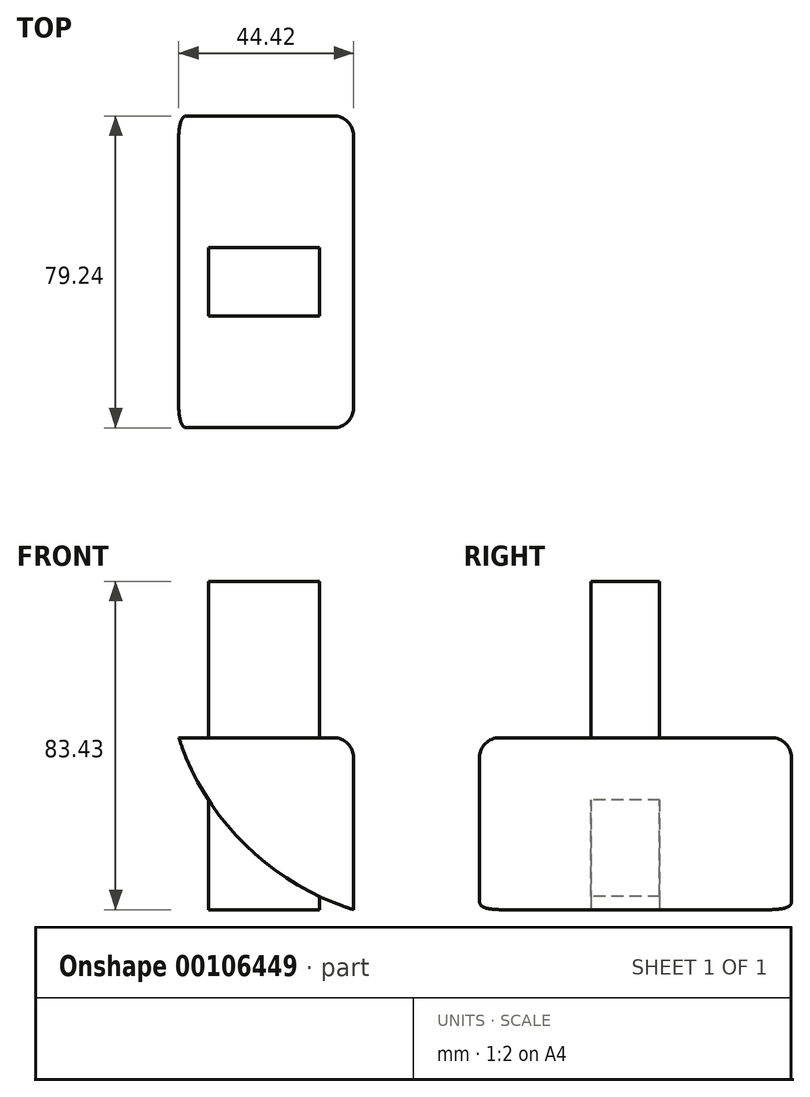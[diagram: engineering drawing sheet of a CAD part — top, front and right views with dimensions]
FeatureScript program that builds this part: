
annotation { "Feature Type Name" : "Feature", "Feature Type Description" : "" }
export const myFeature = defineFeature(function(context is Context, id is Id, definition is map)
    precondition{}
    {
        {
            var Q0;
            Q0=qCreatedBy(makeId("Front.planeOp"),FACE);
            var sketch = newSketch(context, id + "F0", { "sketchPlane" : qUnion([Q0])});
            skLineSegment(sketch, "E0.bottom", {"start": v(-21.73, 0) * mm, "end": v(26.08, 0) * mm});
            skLineSegment(sketch, "E0.top", {"start": v(-21.73, 43.68) * mm, "end": v(26.08, 43.68) * mm});
            skLineSegment(sketch, "E0.left", {"start": v(-21.73, 0) * mm, "end": v(-21.73, 43.68) * mm});
            skLineSegment(sketch, "E0.right", {"start": v(26.08, 0) * mm, "end": v(26.08, 43.68) * mm});
            skSolve(sketch);
        }
        {
            var Q0;
            Q0 = qSketchRegion(id + "F0", true);
            extrude(context, id + "F1", {"entities" : qUnion([Q0]), "depth" : 79.24 * mm});
        }
        {
            var Q0;
            Q0=makeQuery(id+"F1.opExtrude","SWEPT_EDGE",EDGE,{"disambiguationData":[OSD([sQuery(id+"F0.wireOp",EDGE,"E0.bottom"),sQuery(id+"F0.wireOp",EDGE,"E0.left")])]});
            fillet(context, id + "F2", {"entities" : qUnion([Q0]), "radius" : 67.93 * mm, "tangentPropagation" : true, "allowEdgeOverflow" : false});
        }
        {
            var Q0;
            Q0=makeQuery(id+"F1.opExtrude","SWEPT_EDGE",EDGE,{"disambiguationData":[OSD([sQuery(id+"F0.wireOp",EDGE,"E0.top"),sQuery(id+"F0.wireOp",EDGE,"E0.right")])]});
            var Q1;
            Q1=makeQuery(id+"F1.opExtrude","CAP_EDGE",EDGE,{"disambiguationData":[OSD([sQuery(id+"F0.wireOp",EDGE,"E0.top")])],"isStart":false});
            var Q2;
            Q2=makeQuery(id+"F1.opExtrude","CAP_EDGE",EDGE,{"disambiguationData":[OSD([sQuery(id+"F0.wireOp",EDGE,"E0.right")])],"isStart":false});
            var Q3;
            Q3=makeQuery(id+"F1.opExtrude","CAP_EDGE",EDGE,{"disambiguationData":[OSD([sQuery(id+"F0.wireOp",EDGE,"E0.right")])],"isStart":true});
            var Q4;
            Q4=makeQuery(id+"F1.opExtrude","CAP_EDGE",EDGE,{"disambiguationData":[OSD([sQuery(id+"F0.wireOp",EDGE,"E0.top")])],"isStart":true});
            fillet(context, id + "F3", {"entities" : qUnion([Q0, Q1, Q2, Q3, Q4]), "radius" : 5.08 * mm, "tangentPropagation" : true, "allowEdgeOverflow" : false});
        }
        {
            var Q0;
            Q0=qCreatedBy(makeId("Top.planeOp"),FACE);
            var sketch = newSketch(context, id + "F4", { "sketchPlane" : qUnion([Q0])});
            skLineSegment(sketch, "E1.bottom", {"start": v(-10.8, -33.5) * mm, "end": v(17.38, -33.5) * mm});
            skLineSegment(sketch, "E1.top", {"start": v(-10.8, -50.88) * mm, "end": v(17.38, -50.88) * mm});
            skLineSegment(sketch, "E1.left", {"start": v(-10.8, -33.5) * mm, "end": v(-10.8, -50.88) * mm});
            skLineSegment(sketch, "E1.right", {"start": v(17.38, -33.5) * mm, "end": v(17.38, -50.88) * mm});
            skSolve(sketch);
        }
        {
            var Q0;
            Q0 = qSketchRegion(id + "F4", true);
            extrude(context, id + "F5", {"entities" : qUnion([Q0]), "operationType" : NewBodyOperationType.ADD, "depth" : 83.43 * mm});
        }
    });
